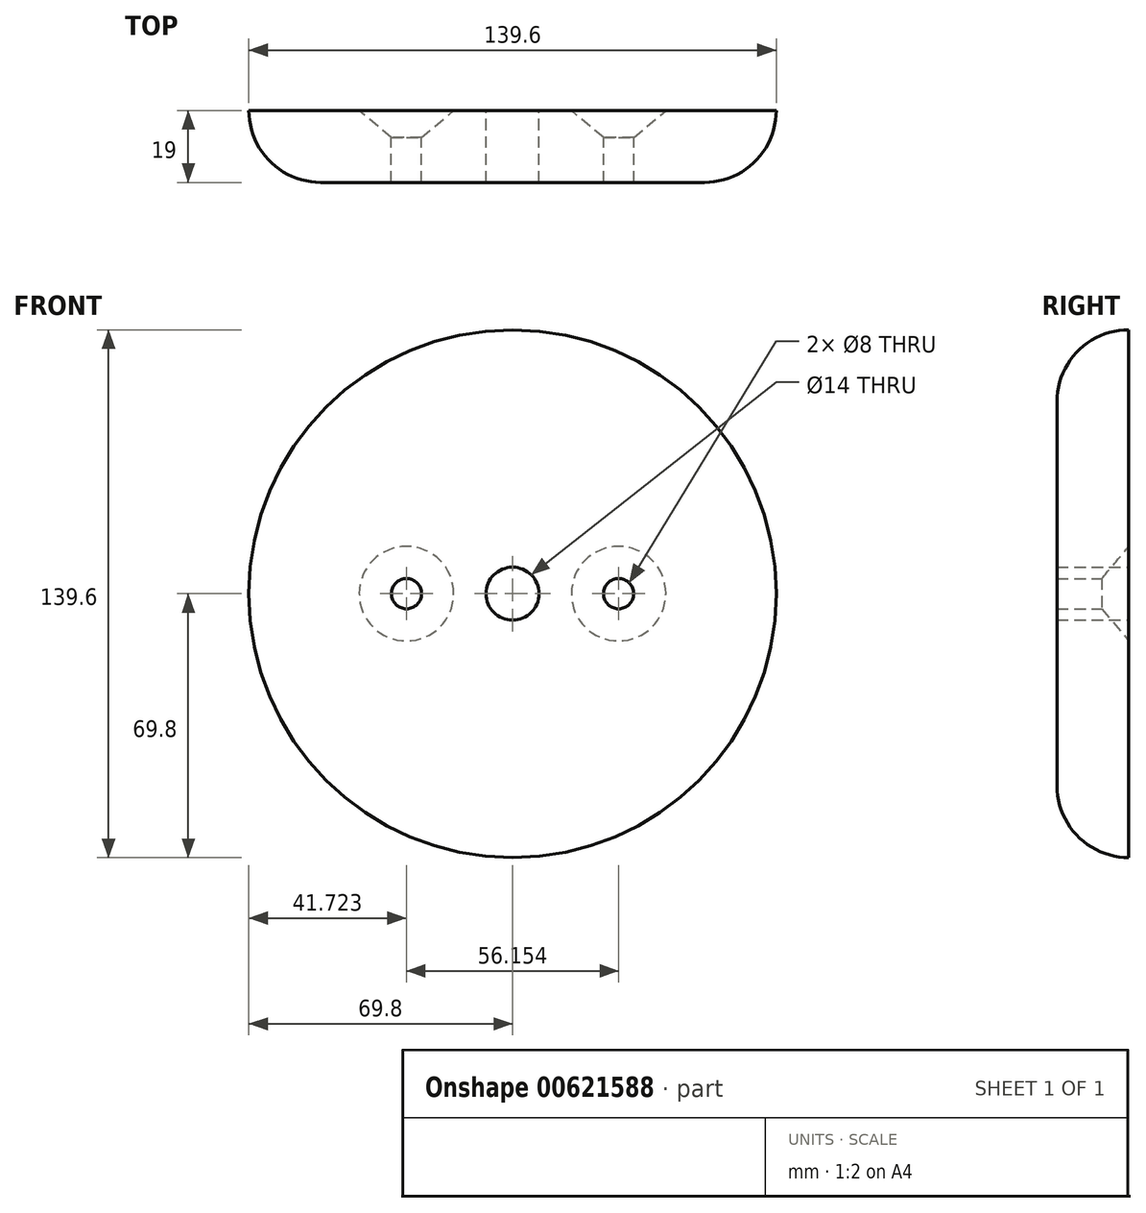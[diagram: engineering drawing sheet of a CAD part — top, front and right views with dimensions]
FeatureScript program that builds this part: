
annotation { "Feature Type Name" : "Feature", "Feature Type Description" : "" }
export const myFeature = defineFeature(function(context is Context, id is Id, definition is map)
    precondition{}
    {
        {
            var Q0;
            Q0=qCreatedBy(makeId("Front.planeOp"),FACE);
            var sketch = newSketch(context, id + "F0", { "sketchPlane" : qUnion([Q0])});
            skCircle(sketch, "E0", {"center": v(0, 0) * mm, "radius": 69.8 * mm});
            skCircle(sketch, "E1", {"center": v(-28.08, 0) * mm, "radius": 5 * mm});
            skCircle(sketch, "E2", {"center": v(28.08, 0) * mm, "radius": 5 * mm});
            skCircle(sketch, "E3", {"center": v(0, 0) * mm, "radius": 50.8 * mm, "construction": true});
            skSolve(sketch);
        }
        {
            var Q0;
            Q0=makeQuery(id+"F0.imprint","IMPRINT",FACE,{"disambiguationData":[TD([[makeQuery(id+"F0.imprint","IMPRINT",EDGE,{"derivedFrom":sQuery(id+"F0.wireOp",EDGE,"E0")}),1.0]])]});
            var Q1;
            Q1=makeQuery(id+"F0.imprint","IMPRINT",FACE,{"disambiguationData":[TD([[makeQuery(id+"F0.imprint","IMPRINT",EDGE,{"derivedFrom":sQuery(id+"F0.wireOp",EDGE,"E1")}),1.0]])]});
            var Q2;
            Q2=makeQuery(id+"F0.imprint","IMPRINT",FACE,{"disambiguationData":[TD([[makeQuery(id+"F0.imprint","IMPRINT",EDGE,{"derivedFrom":sQuery(id+"F0.wireOp",EDGE,"E2")}),1.0]])]});
            extrude(context, id + "F1", {"entities" : qUnion([Q0, Q1, Q2]), "depth" : 19 * mm, "offsetDistance" : 25.4 * mm});
        }
        {
            var Q0;
            Q0=makeQuery(id+"F1.opExtrude","CAP_EDGE",EDGE,{"disambiguationData":[OSD([sQuery(id+"F0.wireOp",EDGE,"E0")])],"isStart":false});
            fillet(context, id + "F2", {"entities" : qUnion([Q0]), "radius" : 19 * mm, "tangentPropagation" : true, "allowEdgeOverflow" : false});
        }
        {
            var Q0;
            Q0=sQuery(id+"F0.wireOp",VERTEX,"E0.center");
            var Q1;
            Q1=makeQuery(id+"F1.opExtrude","SWEPT_BODY",BODY,{"disambiguationData":[OSD([sQuery(id+"F0.wireOp",EDGE,"E0")])]});
            hole(context, id + "F3", {"style" : HoleStyle.SIMPLE, "endStyle" : HoleEndStyle.BLIND, "oppositeDirection" : true, "holeDiameter" : 14 * mm, "majorDiameter" : 12.7 * mm, "holeDepth" : 20 * mm, "isTappedThrough" : true, "tappedDepth" : 12.7 * mm, "tapClearance" : 3, "locations" : qUnion([Q0]), "scope" : qUnion([Q1])});
        }
        {
            var Q0;
            Q0=sQuery(id+"F0.wireOp",VERTEX,"E2.center");
            var Q1;
            Q1=sQuery(id+"F0.wireOp",VERTEX,"E1.center");
            var Q2;
            Q2=makeQuery(id+"F1.opExtrude","SWEPT_BODY",BODY,{"disambiguationData":[OSD([sQuery(id+"F0.wireOp",EDGE,"E0"),sQuery(id+"F0.wireOp",EDGE,"E1"),sQuery(id+"F0.wireOp",EDGE,"E2")])]});
            hole(context, id + "F4", {"style" : HoleStyle.C_SINK, "endStyle" : HoleEndStyle.BLIND, "oppositeDirection" : true, "holeDiameter" : 8 * mm, "cSinkDiameter" : 25 * mm, "cSinkAngle" : 100 * degree, "majorDiameter" : 6.35 * mm, "holeDepth" : 20 * mm, "isTappedThrough" : true, "tappedDepth" : 12.7 * mm, "tapClearance" : 3, "locations" : qUnion([Q0, Q1]), "scope" : qUnion([Q2])});
        }
    });
